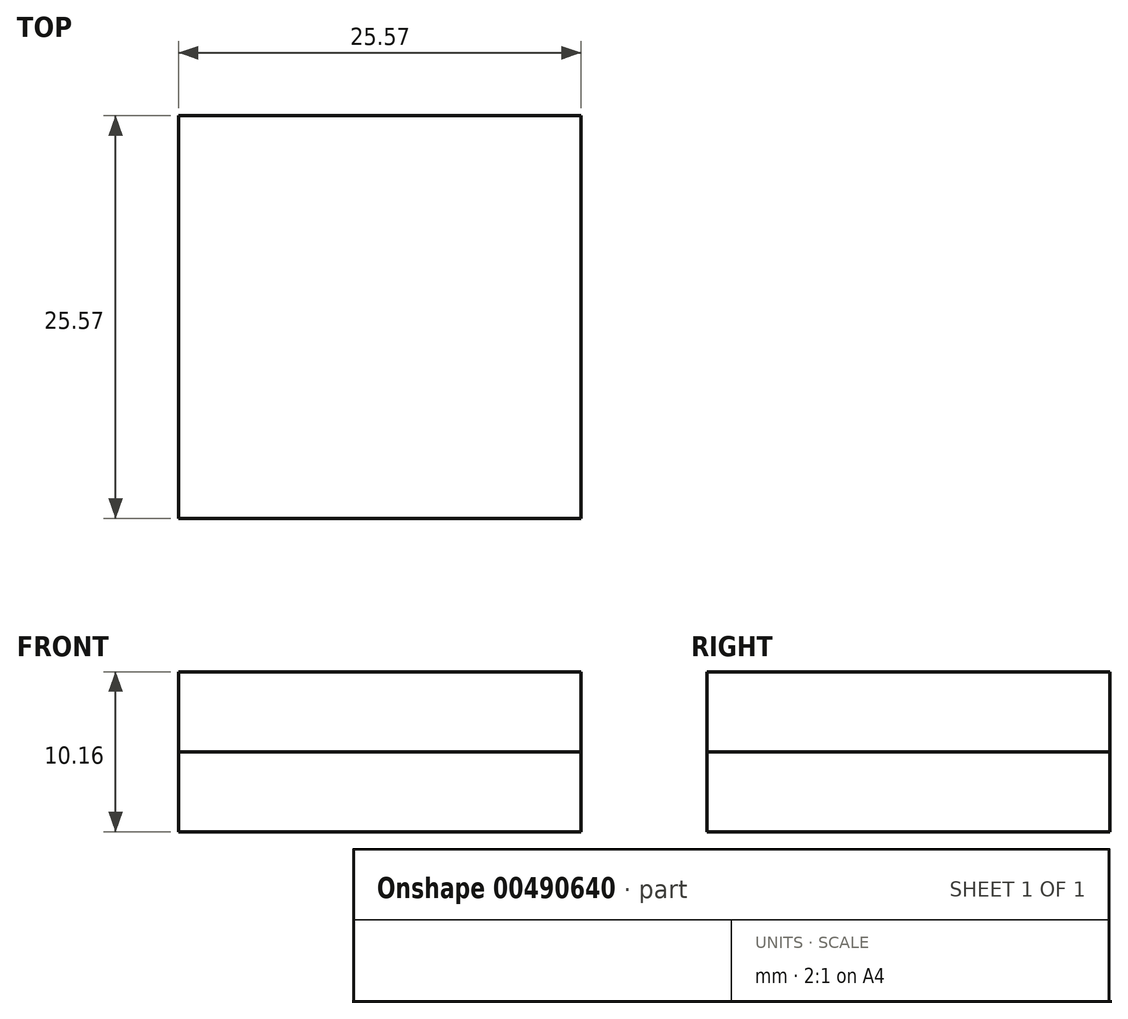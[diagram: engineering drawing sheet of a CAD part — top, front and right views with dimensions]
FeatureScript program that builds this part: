
annotation { "Feature Type Name" : "Feature", "Feature Type Description" : "" }
export const myFeature = defineFeature(function(context is Context, id is Id, definition is map)
    precondition{}
    {
        {
            var Q0;
            Q0=qCreatedBy(makeId("Top.planeOp"),FACE);
            var sketch = newSketch(context, id + "F0", { "sketchPlane" : qUnion([Q0])});
            skLineSegment(sketch, "E0.bottom", {"start": v(0, 0) * mm, "end": v(-25.57, 0) * mm});
            skLineSegment(sketch, "E0.top", {"start": v(0, 25.57) * mm, "end": v(-25.57, 25.57) * mm});
            skLineSegment(sketch, "E0.left", {"start": v(0, 0) * mm, "end": v(0, 25.57) * mm});
            skLineSegment(sketch, "E0.right", {"start": v(-25.57, 0) * mm, "end": v(-25.57, 25.57) * mm});
            skSolve(sketch);
        }
        {
            var Q0;
            Q0=makeQuery(id+"F0.imprint","IMPRINT",FACE,{"disambiguationData":[TD([[makeQuery(id+"F0.imprint","IMPRINT",EDGE,{"derivedFrom":sQuery(id+"F0.wireOp",EDGE,"E0.bottom")}),-1.0]])]});
            extrude(context, id + "F1", {"entities" : qUnion([Q0]), "depth" : 5.08 * mm, "offsetDistance" : 25.4 * mm});
        }
        {
            var Q0;
            Q0=makeQuery(id+"F1.opExtrude","CAP_FACE",FACE,{"disambiguationData":[OSD([sQuery(id+"F0.wireOp",EDGE,"E0.bottom"),sQuery(id+"F0.wireOp",EDGE,"E0.top"),sQuery(id+"F0.wireOp",EDGE,"E0.left"),sQuery(id+"F0.wireOp",EDGE,"E0.right")])],"isStart":false});
            extrude(context, id + "F2", {"entities" : qUnion([Q0]), "depth" : 5.08 * mm, "offsetDistance" : 25.4 * mm});
        }
    });
